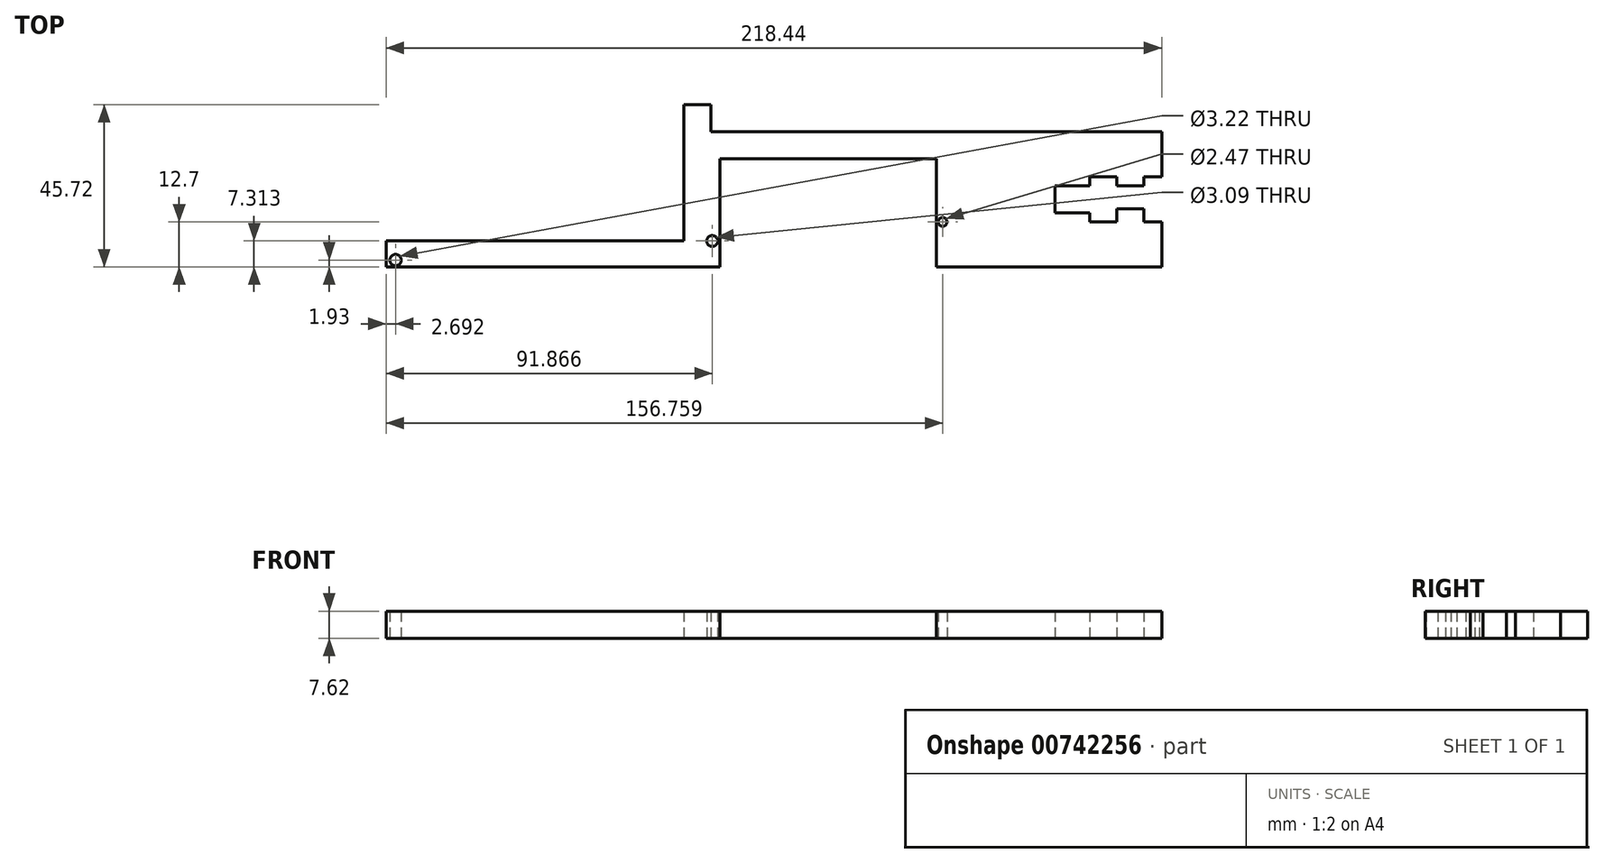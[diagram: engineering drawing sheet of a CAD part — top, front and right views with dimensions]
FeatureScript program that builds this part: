
annotation { "Feature Type Name" : "Feature", "Feature Type Description" : "" }
export const myFeature = defineFeature(function(context is Context, id is Id, definition is map)
    precondition{}
    {
        {
            var Q0;
            Q0=qCreatedBy(makeId("Top.planeOp"),FACE);
            var sketch = newSketch(context, id + "F0", { "sketchPlane" : qUnion([Q0])});
            skLineSegment(sketch, "E0", {"start": v(-72.96, -45.72) * mm, "end": v(21.02, -45.72) * mm});
            skLineSegment(sketch, "E1", {"start": v(21.02, -45.72) * mm, "end": v(21.02, -15.24) * mm});
            skLineSegment(sketch, "E2", {"start": v(21.02, -15.24) * mm, "end": v(81.98, -15.24) * mm});
            skLineSegment(sketch, "E3", {"start": v(81.98, -15.24) * mm, "end": v(81.98, -45.72) * mm});
            skLineSegment(sketch, "E4", {"start": v(81.98, -45.72) * mm, "end": v(145.48, -45.72) * mm});
            skLineSegment(sketch, "E5", {"start": v(145.48, -45.72) * mm, "end": v(145.48, -33.02) * mm});
            skLineSegment(sketch, "E6", {"start": v(145.48, -33.02) * mm, "end": v(140.4, -33.02) * mm});
            skLineSegment(sketch, "E7", {"start": v(132.78, -33.02) * mm, "end": v(125.16, -33.02) * mm});
            skLineSegment(sketch, "E8", {"start": v(125.16, -33.02) * mm, "end": v(125.16, -30.48) * mm});
            skLineSegment(sketch, "E9", {"start": v(125.16, -30.48) * mm, "end": v(115.43, -30.48) * mm});
            skLineSegment(sketch, "E10", {"start": v(115.43, -30.48) * mm, "end": v(115.43, -22.86) * mm});
            skLineSegment(sketch, "E11", {"start": v(115.43, -22.86) * mm, "end": v(125.16, -22.86) * mm});
            skLineSegment(sketch, "E12", {"start": v(125.16, -22.86) * mm, "end": v(125.16, -20.32) * mm});
            skLineSegment(sketch, "E13", {"start": v(125.16, -20.32) * mm, "end": v(132.78, -20.32) * mm});
            skLineSegment(sketch, "E14", {"start": v(132.78, -20.32) * mm, "end": v(132.78, -22.86) * mm});
            skLineSegment(sketch, "E15", {"start": v(132.78, -22.86) * mm, "end": v(140.4, -22.86) * mm});
            skLineSegment(sketch, "E16", {"start": v(140.4, -33.02) * mm, "end": v(140.4, -29.39) * mm});
            skLineSegment(sketch, "E17", {"start": v(140.4, -29.39) * mm, "end": v(132.78, -29.39) * mm});
            skLineSegment(sketch, "E18", {"start": v(132.78, -29.39) * mm, "end": v(132.78, -33.02) * mm});
            skLineSegment(sketch, "E19", {"start": v(140.4, -22.86) * mm, "end": v(140.4, -20.32) * mm});
            skLineSegment(sketch, "E20", {"start": v(140.4, -20.32) * mm, "end": v(145.48, -20.32) * mm});
            skLineSegment(sketch, "E21", {"start": v(145.48, -20.32) * mm, "end": v(145.48, -7.62) * mm});
            skLineSegment(sketch, "E22", {"start": v(145.48, -7.62) * mm, "end": v(18.48, -7.62) * mm});
            skLineSegment(sketch, "E23", {"start": v(18.48, -7.62) * mm, "end": v(18.48, 0) * mm});
            skLineSegment(sketch, "E24", {"start": v(18.48, 0) * mm, "end": v(10.86, 0) * mm});
            skLineSegment(sketch, "E25", {"start": v(10.86, 0) * mm, "end": v(10.86, -7.62) * mm});
            skLineSegment(sketch, "E26", {"start": v(10.86, -7.62) * mm, "end": v(10.86, -38.4) * mm});
            skLineSegment(sketch, "E27", {"start": v(10.86, -38.4) * mm, "end": v(-72.96, -38.4) * mm});
            skLineSegment(sketch, "E28", {"start": v(-72.96, -38.4) * mm, "end": v(-72.96, -45.72) * mm});
            skCircle(sketch, "E29", {"center": v(-70.27, -43.8) * mm, "radius": 1.6 * mm});
            skCircle(sketch, "E30", {"center": v(83.8, -33.02) * mm, "radius": 1.23 * mm});
            skCircle(sketch, "E31", {"center": v(18.9, -38.4) * mm, "radius": 1.54 * mm});
            skSolve(sketch);
        }
        {
            var Q0;
            Q0 = qSketchRegion(id + "F0", true);
            extrude(context, id + "F1", {"entities" : qUnion([Q0]), "depth" : 7.62 * mm, "offsetDistance" : 25.4 * mm});
        }
    });
